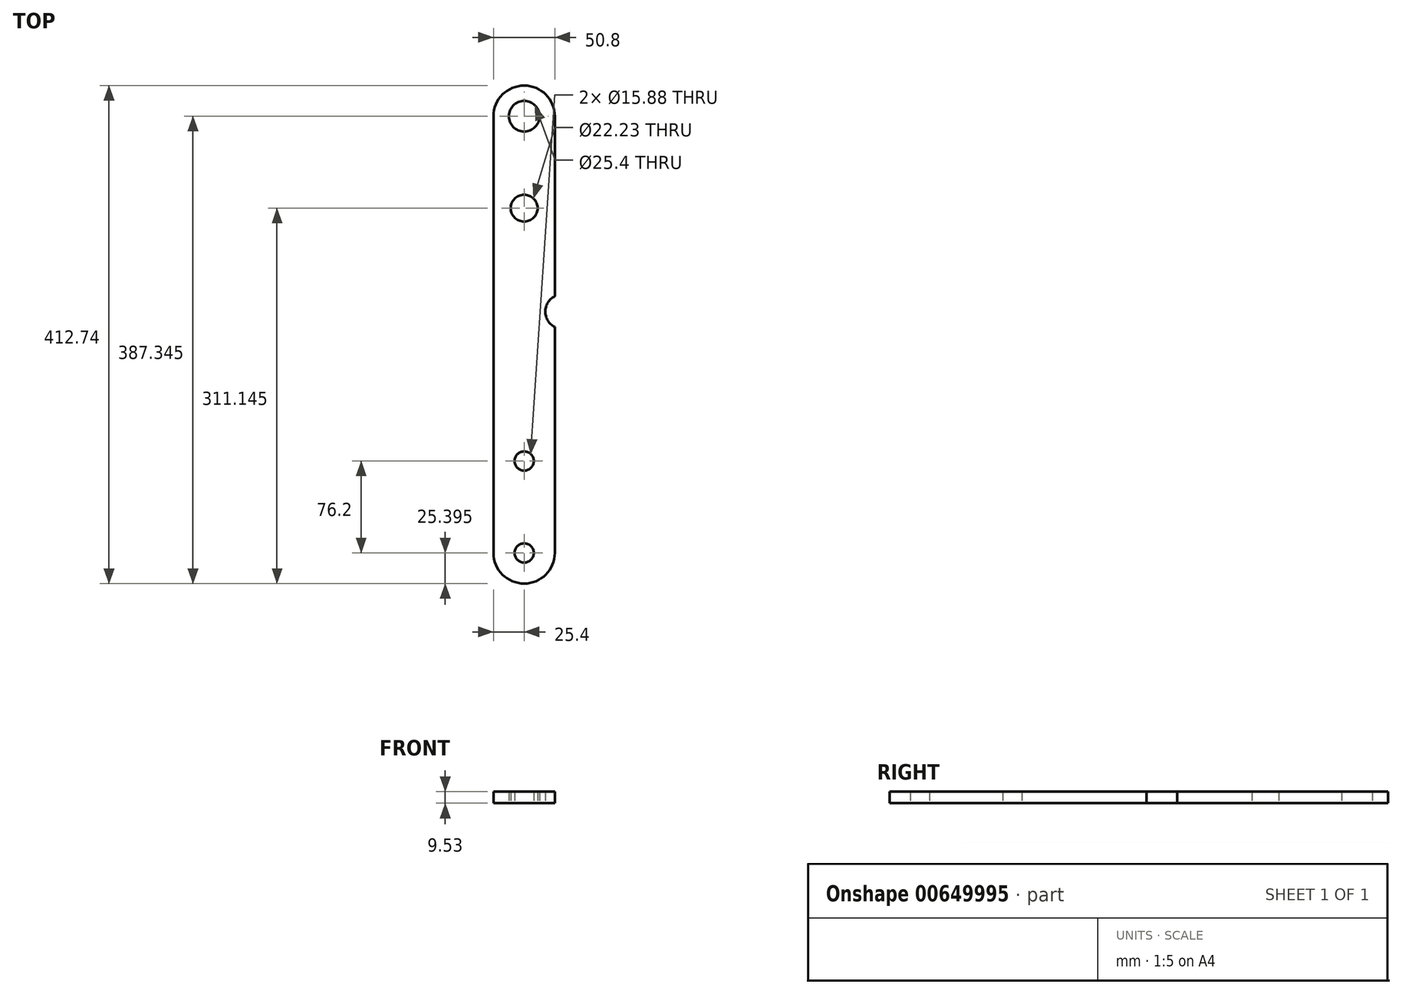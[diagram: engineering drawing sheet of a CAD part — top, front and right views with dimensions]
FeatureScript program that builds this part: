
annotation { "Feature Type Name" : "Feature", "Feature Type Description" : "" }
export const myFeature = defineFeature(function(context is Context, id is Id, definition is map)
    precondition{}
    {
        {
            var Q0;
            Q0=qCreatedBy(makeId("Top.planeOp"),FACE);
            var sketch = newSketch(context, id + "F0", { "sketchPlane" : qUnion([Q0])});
            skLineSegment(sketch, "E0", {"start": v(25.4, 180.98) * mm, "end": v(25.36, 182.46) * mm});
            skLineSegment(sketch, "E1", {"start": v(25.36, 182.46) * mm, "end": v(25.23, 183.94) * mm});
            skLineSegment(sketch, "E2", {"start": v(25.23, 183.94) * mm, "end": v(25.02, 185.4) * mm});
            skLineSegment(sketch, "E3", {"start": v(25.02, 185.4) * mm, "end": v(24.72, 186.84) * mm});
            skLineSegment(sketch, "E4", {"start": v(24.72, 186.84) * mm, "end": v(24.34, 188.26) * mm});
            skLineSegment(sketch, "E5", {"start": v(24.34, 188.26) * mm, "end": v(23.88, 189.67) * mm});
            skLineSegment(sketch, "E6", {"start": v(23.88, 189.67) * mm, "end": v(23.33, 191.05) * mm});
            skLineSegment(sketch, "E7", {"start": v(23.33, 191.05) * mm, "end": v(22.71, 192.38) * mm});
            skLineSegment(sketch, "E8", {"start": v(22.71, 192.38) * mm, "end": v(22, 193.68) * mm});
            skLineSegment(sketch, "E9", {"start": v(22, 193.68) * mm, "end": v(21.23, 194.94) * mm});
            skLineSegment(sketch, "E10", {"start": v(21.23, 194.94) * mm, "end": v(20.38, 196.15) * mm});
            skLineSegment(sketch, "E11", {"start": v(20.38, 196.15) * mm, "end": v(19.45, 197.32) * mm});
            skLineSegment(sketch, "E12", {"start": v(19.45, 197.32) * mm, "end": v(18.48, 198.42) * mm});
            skLineSegment(sketch, "E13", {"start": v(18.48, 198.42) * mm, "end": v(17.44, 199.45) * mm});
            skLineSegment(sketch, "E14", {"start": v(17.44, 199.45) * mm, "end": v(16.34, 200.45) * mm});
            skLineSegment(sketch, "E15", {"start": v(16.34, 200.45) * mm, "end": v(15.18, 201.36) * mm});
            skLineSegment(sketch, "E16", {"start": v(15.18, 201.36) * mm, "end": v(13.97, 202.2) * mm});
            skLineSegment(sketch, "E17", {"start": v(13.97, 202.2) * mm, "end": v(12.7, 202.97) * mm});
            skLineSegment(sketch, "E18", {"start": v(12.7, 202.97) * mm, "end": v(11.4, 203.69) * mm});
            skLineSegment(sketch, "E19", {"start": v(11.4, 203.69) * mm, "end": v(10.08, 204.3) * mm});
            skLineSegment(sketch, "E20", {"start": v(10.08, 204.3) * mm, "end": v(8.7, 204.85) * mm});
            skLineSegment(sketch, "E21", {"start": v(8.7, 204.85) * mm, "end": v(7.28, 205.32) * mm});
            skLineSegment(sketch, "E22", {"start": v(7.28, 205.32) * mm, "end": v(5.86, 205.7) * mm});
            skLineSegment(sketch, "E23", {"start": v(5.86, 205.7) * mm, "end": v(4.42, 206) * mm});
            skLineSegment(sketch, "E24", {"start": v(4.42, 206) * mm, "end": v(2.96, 206.2) * mm});
            skLineSegment(sketch, "E25", {"start": v(2.96, 206.2) * mm, "end": v(1.48, 206.33) * mm});
            skLineSegment(sketch, "E26", {"start": v(1.48, 206.33) * mm, "end": v(0, 206.38) * mm});
            skLineSegment(sketch, "E27", {"start": v(0, 206.38) * mm, "end": v(-1.48, 206.33) * mm});
            skLineSegment(sketch, "E28", {"start": v(-1.48, 206.33) * mm, "end": v(-2.94, 206.2) * mm});
            skLineSegment(sketch, "E29", {"start": v(-2.94, 206.2) * mm, "end": v(-4.4, 206) * mm});
            skLineSegment(sketch, "E30", {"start": v(-4.4, 206) * mm, "end": v(-5.86, 205.7) * mm});
            skLineSegment(sketch, "E31", {"start": v(-5.86, 205.7) * mm, "end": v(-7.28, 205.32) * mm});
            skLineSegment(sketch, "E32", {"start": v(-7.28, 205.32) * mm, "end": v(-8.68, 204.85) * mm});
            skLineSegment(sketch, "E33", {"start": v(-8.68, 204.85) * mm, "end": v(-10.05, 204.3) * mm});
            skLineSegment(sketch, "E34", {"start": v(-10.05, 204.3) * mm, "end": v(-11.39, 203.69) * mm});
            skLineSegment(sketch, "E35", {"start": v(-11.39, 203.69) * mm, "end": v(-12.7, 202.97) * mm});
            skLineSegment(sketch, "E36", {"start": v(-12.7, 202.97) * mm, "end": v(-13.95, 202.2) * mm});
            skLineSegment(sketch, "E37", {"start": v(-13.95, 202.2) * mm, "end": v(-15.16, 201.36) * mm});
            skLineSegment(sketch, "E38", {"start": v(-15.16, 201.36) * mm, "end": v(-16.32, 200.45) * mm});
            skLineSegment(sketch, "E39", {"start": v(-16.32, 200.45) * mm, "end": v(-17.42, 199.45) * mm});
            skLineSegment(sketch, "E40", {"start": v(-17.42, 199.45) * mm, "end": v(-18.48, 198.42) * mm});
            skLineSegment(sketch, "E41", {"start": v(-18.48, 198.42) * mm, "end": v(-19.45, 197.32) * mm});
            skLineSegment(sketch, "E42", {"start": v(-19.45, 197.32) * mm, "end": v(-20.36, 196.15) * mm});
            skLineSegment(sketch, "E43", {"start": v(-20.36, 196.15) * mm, "end": v(-21.2, 194.94) * mm});
            skLineSegment(sketch, "E44", {"start": v(-21.2, 194.94) * mm, "end": v(-22, 193.68) * mm});
            skLineSegment(sketch, "E45", {"start": v(-22, 193.68) * mm, "end": v(-22.7, 192.38) * mm});
            skLineSegment(sketch, "E46", {"start": v(-22.7, 192.38) * mm, "end": v(-23.33, 191.05) * mm});
            skLineSegment(sketch, "E47", {"start": v(-23.33, 191.05) * mm, "end": v(-23.85, 189.67) * mm});
            skLineSegment(sketch, "E48", {"start": v(-23.85, 189.67) * mm, "end": v(-24.32, 188.26) * mm});
            skLineSegment(sketch, "E49", {"start": v(-24.32, 188.26) * mm, "end": v(-24.7, 186.84) * mm});
            skLineSegment(sketch, "E50", {"start": v(-24.7, 186.84) * mm, "end": v(-25.02, 185.4) * mm});
            skLineSegment(sketch, "E51", {"start": v(-25.02, 185.4) * mm, "end": v(-25.23, 183.94) * mm});
            skLineSegment(sketch, "E52", {"start": v(-25.23, 183.94) * mm, "end": v(-25.36, 182.46) * mm});
            skLineSegment(sketch, "E53", {"start": v(-25.36, 182.46) * mm, "end": v(-25.4, 180.98) * mm});
            skLineSegment(sketch, "E54", {"start": v(0, 168.28) * mm, "end": v(1.06, 168.32) * mm});
            skLineSegment(sketch, "E55", {"start": v(1.06, 168.32) * mm, "end": v(2.1, 168.44) * mm});
            skLineSegment(sketch, "E56", {"start": v(2.1, 168.44) * mm, "end": v(3.11, 168.68) * mm});
            skLineSegment(sketch, "E57", {"start": v(3.11, 168.68) * mm, "end": v(4.13, 168.97) * mm});
            skLineSegment(sketch, "E58", {"start": v(4.13, 168.97) * mm, "end": v(5.1, 169.35) * mm});
            skLineSegment(sketch, "E59", {"start": v(5.1, 169.35) * mm, "end": v(6.05, 169.82) * mm});
            skLineSegment(sketch, "E60", {"start": v(6.05, 169.82) * mm, "end": v(6.94, 170.35) * mm});
            skLineSegment(sketch, "E61", {"start": v(6.94, 170.35) * mm, "end": v(7.81, 170.96) * mm});
            skLineSegment(sketch, "E62", {"start": v(7.81, 170.96) * mm, "end": v(8.61, 171.64) * mm});
            skLineSegment(sketch, "E63", {"start": v(8.61, 171.64) * mm, "end": v(9.36, 172.38) * mm});
            skLineSegment(sketch, "E64", {"start": v(9.36, 172.38) * mm, "end": v(10.03, 173.19) * mm});
            skLineSegment(sketch, "E65", {"start": v(10.03, 173.19) * mm, "end": v(10.65, 174.03) * mm});
            skLineSegment(sketch, "E66", {"start": v(10.65, 174.03) * mm, "end": v(11.18, 174.94) * mm});
            skLineSegment(sketch, "E67", {"start": v(11.18, 174.94) * mm, "end": v(11.64, 175.87) * mm});
            skLineSegment(sketch, "E68", {"start": v(11.64, 175.87) * mm, "end": v(12.02, 176.85) * mm});
            skLineSegment(sketch, "E69", {"start": v(12.02, 176.85) * mm, "end": v(12.32, 177.86) * mm});
            skLineSegment(sketch, "E70", {"start": v(12.32, 177.86) * mm, "end": v(12.53, 178.88) * mm});
            skLineSegment(sketch, "E71", {"start": v(12.53, 178.88) * mm, "end": v(12.66, 179.94) * mm});
            skLineSegment(sketch, "E72", {"start": v(12.66, 179.94) * mm, "end": v(12.7, 180.98) * mm});
            skLineSegment(sketch, "E73", {"start": v(12.7, 180.98) * mm, "end": v(12.66, 182.03) * mm});
            skLineSegment(sketch, "E74", {"start": v(12.66, 182.03) * mm, "end": v(12.53, 183.07) * mm});
            skLineSegment(sketch, "E75", {"start": v(12.53, 183.07) * mm, "end": v(12.32, 184.1) * mm});
            skLineSegment(sketch, "E76", {"start": v(12.32, 184.1) * mm, "end": v(12.02, 185.1) * mm});
            skLineSegment(sketch, "E77", {"start": v(12.02, 185.1) * mm, "end": v(11.64, 186.08) * mm});
            skLineSegment(sketch, "E78", {"start": v(11.64, 186.08) * mm, "end": v(11.18, 187.03) * mm});
            skLineSegment(sketch, "E79", {"start": v(11.18, 187.03) * mm, "end": v(10.65, 187.92) * mm});
            skLineSegment(sketch, "E80", {"start": v(10.65, 187.92) * mm, "end": v(10.03, 188.79) * mm});
            skLineSegment(sketch, "E81", {"start": v(10.03, 188.79) * mm, "end": v(9.36, 189.59) * mm});
            skLineSegment(sketch, "E82", {"start": v(9.36, 189.59) * mm, "end": v(8.61, 190.33) * mm});
            skLineSegment(sketch, "E83", {"start": v(8.61, 190.33) * mm, "end": v(7.81, 191) * mm});
            skLineSegment(sketch, "E84", {"start": v(7.81, 191) * mm, "end": v(6.94, 191.62) * mm});
            skLineSegment(sketch, "E85", {"start": v(6.94, 191.62) * mm, "end": v(6.05, 192.15) * mm});
            skLineSegment(sketch, "E86", {"start": v(6.05, 192.15) * mm, "end": v(5.1, 192.62) * mm});
            skLineSegment(sketch, "E87", {"start": v(5.1, 192.62) * mm, "end": v(4.13, 193) * mm});
            skLineSegment(sketch, "E88", {"start": v(4.13, 193) * mm, "end": v(3.11, 193.3) * mm});
            skLineSegment(sketch, "E89", {"start": v(3.11, 193.3) * mm, "end": v(2.1, 193.5) * mm});
            skLineSegment(sketch, "E90", {"start": v(2.1, 193.5) * mm, "end": v(1.06, 193.63) * mm});
            skLineSegment(sketch, "E91", {"start": v(1.06, 193.63) * mm, "end": v(0, 193.68) * mm});
            skLineSegment(sketch, "E92", {"start": v(0, 193.68) * mm, "end": v(-1.04, 193.63) * mm});
            skLineSegment(sketch, "E93", {"start": v(-1.04, 193.63) * mm, "end": v(-2.1, 193.5) * mm});
            skLineSegment(sketch, "E94", {"start": v(-2.1, 193.5) * mm, "end": v(-3.11, 193.3) * mm});
            skLineSegment(sketch, "E95", {"start": v(-3.11, 193.3) * mm, "end": v(-4.13, 193) * mm});
            skLineSegment(sketch, "E96", {"start": v(-4.13, 193) * mm, "end": v(-5.1, 192.62) * mm});
            skLineSegment(sketch, "E97", {"start": v(-5.1, 192.62) * mm, "end": v(-6.03, 192.15) * mm});
            skLineSegment(sketch, "E98", {"start": v(-6.03, 192.15) * mm, "end": v(-6.94, 191.62) * mm});
            skLineSegment(sketch, "E99", {"start": v(-6.94, 191.62) * mm, "end": v(-7.79, 191) * mm});
            skLineSegment(sketch, "E100", {"start": v(-7.79, 191) * mm, "end": v(-8.6, 190.33) * mm});
            skLineSegment(sketch, "E101", {"start": v(-8.6, 190.33) * mm, "end": v(-9.33, 189.59) * mm});
            skLineSegment(sketch, "E102", {"start": v(-9.33, 189.59) * mm, "end": v(-10.01, 188.79) * mm});
            skLineSegment(sketch, "E103", {"start": v(-10.01, 188.79) * mm, "end": v(-10.63, 187.92) * mm});
            skLineSegment(sketch, "E104", {"start": v(-10.63, 187.92) * mm, "end": v(-11.15, 187.03) * mm});
            skLineSegment(sketch, "E105", {"start": v(-11.15, 187.03) * mm, "end": v(-11.62, 186.08) * mm});
            skLineSegment(sketch, "E106", {"start": v(-11.62, 186.08) * mm, "end": v(-12, 185.1) * mm});
            skLineSegment(sketch, "E107", {"start": v(-12, 185.1) * mm, "end": v(-12.3, 184.1) * mm});
            skLineSegment(sketch, "E108", {"start": v(-12.3, 184.1) * mm, "end": v(-12.53, 183.07) * mm});
            skLineSegment(sketch, "E109", {"start": v(-12.53, 183.07) * mm, "end": v(-12.66, 182.03) * mm});
            skLineSegment(sketch, "E110", {"start": v(-12.66, 182.03) * mm, "end": v(-12.7, 180.98) * mm});
            skLineSegment(sketch, "E111", {"start": v(-12.7, 180.98) * mm, "end": v(-12.66, 179.94) * mm});
            skLineSegment(sketch, "E112", {"start": v(-12.66, 179.94) * mm, "end": v(-12.53, 178.88) * mm});
            skLineSegment(sketch, "E113", {"start": v(-12.53, 178.88) * mm, "end": v(-12.3, 177.86) * mm});
            skLineSegment(sketch, "E114", {"start": v(-12.3, 177.86) * mm, "end": v(-12, 176.85) * mm});
            skLineSegment(sketch, "E115", {"start": v(-12, 176.85) * mm, "end": v(-11.62, 175.87) * mm});
            skLineSegment(sketch, "E116", {"start": v(-11.62, 175.87) * mm, "end": v(-11.15, 174.94) * mm});
            skLineSegment(sketch, "E117", {"start": v(-11.15, 174.94) * mm, "end": v(-10.63, 174.03) * mm});
            skLineSegment(sketch, "E118", {"start": v(-10.63, 174.03) * mm, "end": v(-10.01, 173.19) * mm});
            skLineSegment(sketch, "E119", {"start": v(-10.01, 173.19) * mm, "end": v(-9.33, 172.38) * mm});
            skLineSegment(sketch, "E120", {"start": v(-9.33, 172.38) * mm, "end": v(-8.6, 171.64) * mm});
            skLineSegment(sketch, "E121", {"start": v(-8.6, 171.64) * mm, "end": v(-7.79, 170.96) * mm});
            skLineSegment(sketch, "E122", {"start": v(-7.79, 170.96) * mm, "end": v(-6.94, 170.35) * mm});
            skLineSegment(sketch, "E123", {"start": v(-6.94, 170.35) * mm, "end": v(-6.03, 169.82) * mm});
            skLineSegment(sketch, "E124", {"start": v(-6.03, 169.82) * mm, "end": v(-5.1, 169.35) * mm});
            skLineSegment(sketch, "E125", {"start": v(-5.1, 169.35) * mm, "end": v(-4.13, 168.97) * mm});
            skLineSegment(sketch, "E126", {"start": v(-4.13, 168.97) * mm, "end": v(-3.11, 168.68) * mm});
            skLineSegment(sketch, "E127", {"start": v(-3.11, 168.68) * mm, "end": v(-2.1, 168.44) * mm});
            skLineSegment(sketch, "E128", {"start": v(-2.1, 168.44) * mm, "end": v(-1.04, 168.32) * mm});
            skLineSegment(sketch, "E129", {"start": v(-1.04, 168.32) * mm, "end": v(0, 168.28) * mm});
            skLineSegment(sketch, "E130", {"start": v(25.4, 6.35) * mm, "end": v(25.4, -180.98) * mm});
            skLineSegment(sketch, "E131", {"start": v(25.4, 180.98) * mm, "end": v(25.4, 31.75) * mm});
            skLineSegment(sketch, "E132", {"start": v(-25.4, 180.98) * mm, "end": v(-25.4, -180.98) * mm});
            skLineSegment(sketch, "E133", {"start": v(0, -188.91) * mm, "end": v(0.83, -188.87) * mm});
            skLineSegment(sketch, "E134", {"start": v(0.83, -188.87) * mm, "end": v(1.65, -188.74) * mm});
            skLineSegment(sketch, "E135", {"start": v(1.65, -188.74) * mm, "end": v(2.46, -188.51) * mm});
            skLineSegment(sketch, "E136", {"start": v(2.46, -188.51) * mm, "end": v(3.24, -188.21) * mm});
            skLineSegment(sketch, "E137", {"start": v(3.24, -188.21) * mm, "end": v(3.98, -187.85) * mm});
            skLineSegment(sketch, "E138", {"start": v(3.98, -187.85) * mm, "end": v(4.68, -187.39) * mm});
            skLineSegment(sketch, "E139", {"start": v(4.68, -187.39) * mm, "end": v(5.31, -186.86) * mm});
            skLineSegment(sketch, "E140", {"start": v(5.31, -186.86) * mm, "end": v(5.9, -186.29) * mm});
            skLineSegment(sketch, "E141", {"start": v(5.9, -186.29) * mm, "end": v(6.43, -185.63) * mm});
            skLineSegment(sketch, "E142", {"start": v(6.43, -185.63) * mm, "end": v(6.88, -184.93) * mm});
            skLineSegment(sketch, "E143", {"start": v(6.88, -184.93) * mm, "end": v(7.26, -184.2) * mm});
            skLineSegment(sketch, "E144", {"start": v(7.26, -184.2) * mm, "end": v(7.56, -183.43) * mm});
            skLineSegment(sketch, "E145", {"start": v(7.56, -183.43) * mm, "end": v(7.77, -182.63) * mm});
            skLineSegment(sketch, "E146", {"start": v(7.77, -182.63) * mm, "end": v(7.9, -181.8) * mm});
            skLineSegment(sketch, "E147", {"start": v(7.9, -181.8) * mm, "end": v(7.94, -180.98) * mm});
            skLineSegment(sketch, "E148", {"start": v(7.94, -180.98) * mm, "end": v(7.9, -180.15) * mm});
            skLineSegment(sketch, "E149", {"start": v(7.9, -180.15) * mm, "end": v(7.77, -179.32) * mm});
            skLineSegment(sketch, "E150", {"start": v(7.77, -179.32) * mm, "end": v(7.56, -178.52) * mm});
            skLineSegment(sketch, "E151", {"start": v(7.56, -178.52) * mm, "end": v(7.26, -177.74) * mm});
            skLineSegment(sketch, "E152", {"start": v(7.26, -177.74) * mm, "end": v(6.88, -177) * mm});
            skLineSegment(sketch, "E153", {"start": v(6.88, -177) * mm, "end": v(6.43, -176.3) * mm});
            skLineSegment(sketch, "E154", {"start": v(6.43, -176.3) * mm, "end": v(5.9, -175.66) * mm});
            skLineSegment(sketch, "E155", {"start": v(5.9, -175.66) * mm, "end": v(5.31, -175.07) * mm});
            skLineSegment(sketch, "E156", {"start": v(5.31, -175.07) * mm, "end": v(4.68, -174.54) * mm});
            skLineSegment(sketch, "E157", {"start": v(4.68, -174.54) * mm, "end": v(3.98, -174.1) * mm});
            skLineSegment(sketch, "E158", {"start": v(3.98, -174.1) * mm, "end": v(3.24, -173.71) * mm});
            skLineSegment(sketch, "E159", {"start": v(3.24, -173.71) * mm, "end": v(2.46, -173.42) * mm});
            skLineSegment(sketch, "E160", {"start": v(2.46, -173.42) * mm, "end": v(1.65, -173.2) * mm});
            skLineSegment(sketch, "E161", {"start": v(1.65, -173.2) * mm, "end": v(0.83, -173.08) * mm});
            skLineSegment(sketch, "E162", {"start": v(0.83, -173.08) * mm, "end": v(0, -173.04) * mm});
            skLineSegment(sketch, "E163", {"start": v(0, -173.04) * mm, "end": v(-0.83, -173.08) * mm});
            skLineSegment(sketch, "E164", {"start": v(-0.83, -173.08) * mm, "end": v(-1.65, -173.2) * mm});
            skLineSegment(sketch, "E165", {"start": v(-1.65, -173.2) * mm, "end": v(-2.46, -173.42) * mm});
            skLineSegment(sketch, "E166", {"start": v(-2.46, -173.42) * mm, "end": v(-3.22, -173.71) * mm});
            skLineSegment(sketch, "E167", {"start": v(-3.22, -173.71) * mm, "end": v(-3.96, -174.1) * mm});
            skLineSegment(sketch, "E168", {"start": v(-3.96, -174.1) * mm, "end": v(-4.66, -174.54) * mm});
            skLineSegment(sketch, "E169", {"start": v(-4.66, -174.54) * mm, "end": v(-5.31, -175.07) * mm});
            skLineSegment(sketch, "E170", {"start": v(-5.31, -175.07) * mm, "end": v(-5.88, -175.66) * mm});
            skLineSegment(sketch, "E171", {"start": v(-5.88, -175.66) * mm, "end": v(-6.41, -176.3) * mm});
            skLineSegment(sketch, "E172", {"start": v(-6.41, -176.3) * mm, "end": v(-6.88, -177) * mm});
            skLineSegment(sketch, "E173", {"start": v(-6.88, -177) * mm, "end": v(-7.24, -177.74) * mm});
            skLineSegment(sketch, "E174", {"start": v(-7.24, -177.74) * mm, "end": v(-7.54, -178.52) * mm});
            skLineSegment(sketch, "E175", {"start": v(-7.54, -178.52) * mm, "end": v(-7.77, -179.32) * mm});
            skLineSegment(sketch, "E176", {"start": v(-7.77, -179.32) * mm, "end": v(-7.9, -180.15) * mm});
            skLineSegment(sketch, "E177", {"start": v(-7.9, -180.15) * mm, "end": v(-7.94, -180.98) * mm});
            skLineSegment(sketch, "E178", {"start": v(-7.94, -180.98) * mm, "end": v(-7.9, -181.8) * mm});
            skLineSegment(sketch, "E179", {"start": v(-7.9, -181.8) * mm, "end": v(-7.77, -182.63) * mm});
            skLineSegment(sketch, "E180", {"start": v(-7.77, -182.63) * mm, "end": v(-7.54, -183.43) * mm});
            skLineSegment(sketch, "E181", {"start": v(-7.54, -183.43) * mm, "end": v(-7.24, -184.2) * mm});
            skLineSegment(sketch, "E182", {"start": v(-7.24, -184.2) * mm, "end": v(-6.88, -184.93) * mm});
            skLineSegment(sketch, "E183", {"start": v(-6.88, -184.93) * mm, "end": v(-6.41, -185.63) * mm});
            skLineSegment(sketch, "E184", {"start": v(-6.41, -185.63) * mm, "end": v(-5.88, -186.29) * mm});
            skLineSegment(sketch, "E185", {"start": v(-5.88, -186.29) * mm, "end": v(-5.31, -186.86) * mm});
            skLineSegment(sketch, "E186", {"start": v(-5.31, -186.86) * mm, "end": v(-4.66, -187.39) * mm});
            skLineSegment(sketch, "E187", {"start": v(-4.66, -187.39) * mm, "end": v(-3.96, -187.85) * mm});
            skLineSegment(sketch, "E188", {"start": v(-3.96, -187.85) * mm, "end": v(-3.22, -188.21) * mm});
            skLineSegment(sketch, "E189", {"start": v(-3.22, -188.21) * mm, "end": v(-2.46, -188.51) * mm});
            skLineSegment(sketch, "E190", {"start": v(-2.46, -188.51) * mm, "end": v(-1.65, -188.74) * mm});
            skLineSegment(sketch, "E191", {"start": v(-1.65, -188.74) * mm, "end": v(-0.83, -188.87) * mm});
            skLineSegment(sketch, "E192", {"start": v(-0.83, -188.87) * mm, "end": v(0, -188.91) * mm});
            skLineSegment(sketch, "E193", {"start": v(-25.4, -180.98) * mm, "end": v(-25.36, -182.46) * mm});
            skLineSegment(sketch, "E194", {"start": v(-25.36, -182.46) * mm, "end": v(-25.23, -183.92) * mm});
            skLineSegment(sketch, "E195", {"start": v(-25.23, -183.92) * mm, "end": v(-25.02, -185.38) * mm});
            skLineSegment(sketch, "E196", {"start": v(-25.02, -185.38) * mm, "end": v(-24.7, -186.82) * mm});
            skLineSegment(sketch, "E197", {"start": v(-24.7, -186.82) * mm, "end": v(-24.32, -188.26) * mm});
            skLineSegment(sketch, "E198", {"start": v(-24.32, -188.26) * mm, "end": v(-23.85, -189.65) * mm});
            skLineSegment(sketch, "E199", {"start": v(-23.85, -189.65) * mm, "end": v(-23.33, -191.03) * mm});
            skLineSegment(sketch, "E200", {"start": v(-23.33, -191.03) * mm, "end": v(-22.7, -192.36) * mm});
            skLineSegment(sketch, "E201", {"start": v(-22.7, -192.36) * mm, "end": v(-22, -193.68) * mm});
            skLineSegment(sketch, "E202", {"start": v(-22, -193.68) * mm, "end": v(-21.2, -194.92) * mm});
            skLineSegment(sketch, "E203", {"start": v(-21.2, -194.92) * mm, "end": v(-20.36, -196.13) * mm});
            skLineSegment(sketch, "E204", {"start": v(-20.36, -196.13) * mm, "end": v(-19.45, -197.3) * mm});
            skLineSegment(sketch, "E205", {"start": v(-19.45, -197.3) * mm, "end": v(-18.48, -198.4) * mm});
            skLineSegment(sketch, "E206", {"start": v(-18.48, -198.4) * mm, "end": v(-17.42, -199.45) * mm});
            skLineSegment(sketch, "E207", {"start": v(-17.42, -199.45) * mm, "end": v(-16.32, -200.43) * mm});
            skLineSegment(sketch, "E208", {"start": v(-16.32, -200.43) * mm, "end": v(-15.16, -201.34) * mm});
            skLineSegment(sketch, "E209", {"start": v(-15.16, -201.34) * mm, "end": v(-13.95, -202.18) * mm});
            skLineSegment(sketch, "E210", {"start": v(-13.95, -202.18) * mm, "end": v(-12.7, -202.97) * mm});
            skLineSegment(sketch, "E211", {"start": v(-12.7, -202.97) * mm, "end": v(-11.39, -203.67) * mm});
            skLineSegment(sketch, "E212", {"start": v(-11.39, -203.67) * mm, "end": v(-10.05, -204.3) * mm});
            skLineSegment(sketch, "E213", {"start": v(-10.05, -204.3) * mm, "end": v(-8.68, -204.83) * mm});
            skLineSegment(sketch, "E214", {"start": v(-8.68, -204.83) * mm, "end": v(-7.28, -205.3) * mm});
            skLineSegment(sketch, "E215", {"start": v(-7.28, -205.3) * mm, "end": v(-5.86, -205.68) * mm});
            skLineSegment(sketch, "E216", {"start": v(-5.86, -205.68) * mm, "end": v(-4.4, -206) * mm});
            skLineSegment(sketch, "E217", {"start": v(-4.4, -206) * mm, "end": v(-2.94, -206.2) * mm});
            skLineSegment(sketch, "E218", {"start": v(-2.94, -206.2) * mm, "end": v(-1.48, -206.33) * mm});
            skLineSegment(sketch, "E219", {"start": v(-1.48, -206.33) * mm, "end": v(0, -206.38) * mm});
            skLineSegment(sketch, "E220", {"start": v(0, -206.38) * mm, "end": v(1.48, -206.33) * mm});
            skLineSegment(sketch, "E221", {"start": v(1.48, -206.33) * mm, "end": v(2.96, -206.2) * mm});
            skLineSegment(sketch, "E222", {"start": v(2.96, -206.2) * mm, "end": v(4.42, -206) * mm});
            skLineSegment(sketch, "E223", {"start": v(4.42, -206) * mm, "end": v(5.86, -205.68) * mm});
            skLineSegment(sketch, "E224", {"start": v(5.86, -205.68) * mm, "end": v(7.28, -205.3) * mm});
            skLineSegment(sketch, "E225", {"start": v(7.28, -205.3) * mm, "end": v(8.7, -204.83) * mm});
            skLineSegment(sketch, "E226", {"start": v(8.7, -204.83) * mm, "end": v(10.08, -204.3) * mm});
            skLineSegment(sketch, "E227", {"start": v(10.08, -204.3) * mm, "end": v(11.4, -203.67) * mm});
            skLineSegment(sketch, "E228", {"start": v(11.4, -203.67) * mm, "end": v(12.7, -202.97) * mm});
            skLineSegment(sketch, "E229", {"start": v(12.7, -202.97) * mm, "end": v(13.97, -202.18) * mm});
            skLineSegment(sketch, "E230", {"start": v(13.97, -202.18) * mm, "end": v(15.18, -201.34) * mm});
            skLineSegment(sketch, "E231", {"start": v(15.18, -201.34) * mm, "end": v(16.34, -200.43) * mm});
            skLineSegment(sketch, "E232", {"start": v(16.34, -200.43) * mm, "end": v(17.44, -199.45) * mm});
            skLineSegment(sketch, "E233", {"start": v(17.44, -199.45) * mm, "end": v(18.48, -198.4) * mm});
            skLineSegment(sketch, "E234", {"start": v(18.48, -198.4) * mm, "end": v(19.45, -197.3) * mm});
            skLineSegment(sketch, "E235", {"start": v(19.45, -197.3) * mm, "end": v(20.38, -196.13) * mm});
            skLineSegment(sketch, "E236", {"start": v(20.38, -196.13) * mm, "end": v(21.23, -194.92) * mm});
            skLineSegment(sketch, "E237", {"start": v(21.23, -194.92) * mm, "end": v(22, -193.68) * mm});
            skLineSegment(sketch, "E238", {"start": v(22, -193.68) * mm, "end": v(22.71, -192.36) * mm});
            skLineSegment(sketch, "E239", {"start": v(22.71, -192.36) * mm, "end": v(23.33, -191.03) * mm});
            skLineSegment(sketch, "E240", {"start": v(23.33, -191.03) * mm, "end": v(23.88, -189.65) * mm});
            skLineSegment(sketch, "E241", {"start": v(23.88, -189.65) * mm, "end": v(24.34, -188.26) * mm});
            skLineSegment(sketch, "E242", {"start": v(24.34, -188.26) * mm, "end": v(24.72, -186.82) * mm});
            skLineSegment(sketch, "E243", {"start": v(24.72, -186.82) * mm, "end": v(25.02, -185.38) * mm});
            skLineSegment(sketch, "E244", {"start": v(25.02, -185.38) * mm, "end": v(25.23, -183.92) * mm});
            skLineSegment(sketch, "E245", {"start": v(25.23, -183.92) * mm, "end": v(25.36, -182.46) * mm});
            skLineSegment(sketch, "E246", {"start": v(25.36, -182.46) * mm, "end": v(25.4, -180.98) * mm});
            skLineSegment(sketch, "E247", {"start": v(0, 93.66) * mm, "end": v(0.97, 93.7) * mm});
            skLineSegment(sketch, "E248", {"start": v(0.97, 93.7) * mm, "end": v(1.93, 93.83) * mm});
            skLineSegment(sketch, "E249", {"start": v(1.93, 93.83) * mm, "end": v(2.88, 94.04) * mm});
            skLineSegment(sketch, "E250", {"start": v(2.88, 94.04) * mm, "end": v(3.8, 94.34) * mm});
            skLineSegment(sketch, "E251", {"start": v(3.8, 94.34) * mm, "end": v(4.7, 94.7) * mm});
            skLineSegment(sketch, "E252", {"start": v(4.7, 94.7) * mm, "end": v(5.57, 95.17) * mm});
            skLineSegment(sketch, "E253", {"start": v(5.57, 95.17) * mm, "end": v(6.37, 95.67) * mm});
            skLineSegment(sketch, "E254", {"start": v(6.37, 95.67) * mm, "end": v(7.15, 96.27) * mm});
            skLineSegment(sketch, "E255", {"start": v(7.15, 96.27) * mm, "end": v(7.85, 96.92) * mm});
            skLineSegment(sketch, "E256", {"start": v(7.85, 96.92) * mm, "end": v(8.5, 97.64) * mm});
            skLineSegment(sketch, "E257", {"start": v(8.5, 97.64) * mm, "end": v(9.1, 98.4) * mm});
            skLineSegment(sketch, "E258", {"start": v(9.1, 98.4) * mm, "end": v(9.63, 99.23) * mm});
            skLineSegment(sketch, "E259", {"start": v(9.63, 99.23) * mm, "end": v(10.08, 100.08) * mm});
            skLineSegment(sketch, "E260", {"start": v(10.08, 100.08) * mm, "end": v(10.46, 100.99) * mm});
            skLineSegment(sketch, "E261", {"start": v(10.46, 100.99) * mm, "end": v(10.73, 101.9) * mm});
            skLineSegment(sketch, "E262", {"start": v(10.73, 101.9) * mm, "end": v(10.94, 102.85) * mm});
            skLineSegment(sketch, "E263", {"start": v(10.94, 102.85) * mm, "end": v(11.07, 103.8) * mm});
            skLineSegment(sketch, "E264", {"start": v(11.07, 103.8) * mm, "end": v(11.11, 104.78) * mm});
            skLineSegment(sketch, "E265", {"start": v(11.11, 104.78) * mm, "end": v(11.07, 105.75) * mm});
            skLineSegment(sketch, "E266", {"start": v(11.07, 105.75) * mm, "end": v(10.94, 106.7) * mm});
            skLineSegment(sketch, "E267", {"start": v(10.94, 106.7) * mm, "end": v(10.73, 107.65) * mm});
            skLineSegment(sketch, "E268", {"start": v(10.73, 107.65) * mm, "end": v(10.46, 108.59) * mm});
            skLineSegment(sketch, "E269", {"start": v(10.46, 108.59) * mm, "end": v(10.08, 109.47) * mm});
            skLineSegment(sketch, "E270", {"start": v(10.08, 109.47) * mm, "end": v(9.63, 110.34) * mm});
            skLineSegment(sketch, "E271", {"start": v(9.63, 110.34) * mm, "end": v(9.1, 111.15) * mm});
            skLineSegment(sketch, "E272", {"start": v(9.1, 111.15) * mm, "end": v(8.5, 111.93) * mm});
            skLineSegment(sketch, "E273", {"start": v(8.5, 111.93) * mm, "end": v(7.85, 112.63) * mm});
            skLineSegment(sketch, "E274", {"start": v(7.85, 112.63) * mm, "end": v(7.15, 113.28) * mm});
            skLineSegment(sketch, "E275", {"start": v(7.15, 113.28) * mm, "end": v(6.37, 113.88) * mm});
            skLineSegment(sketch, "E276", {"start": v(6.37, 113.88) * mm, "end": v(5.57, 114.4) * mm});
            skLineSegment(sketch, "E277", {"start": v(5.57, 114.4) * mm, "end": v(4.7, 114.85) * mm});
            skLineSegment(sketch, "E278", {"start": v(4.7, 114.85) * mm, "end": v(3.8, 115.23) * mm});
            skLineSegment(sketch, "E279", {"start": v(3.8, 115.23) * mm, "end": v(2.88, 115.5) * mm});
            skLineSegment(sketch, "E280", {"start": v(2.88, 115.5) * mm, "end": v(1.93, 115.72) * mm});
            skLineSegment(sketch, "E281", {"start": v(1.93, 115.72) * mm, "end": v(0.97, 115.85) * mm});
            skLineSegment(sketch, "E282", {"start": v(0.97, 115.85) * mm, "end": v(0, 115.89) * mm});
            skLineSegment(sketch, "E283", {"start": v(0, 115.89) * mm, "end": v(-0.97, 115.85) * mm});
            skLineSegment(sketch, "E284", {"start": v(-0.97, 115.85) * mm, "end": v(-1.93, 115.72) * mm});
            skLineSegment(sketch, "E285", {"start": v(-1.93, 115.72) * mm, "end": v(-2.88, 115.5) * mm});
            skLineSegment(sketch, "E286", {"start": v(-2.88, 115.5) * mm, "end": v(-3.79, 115.23) * mm});
            skLineSegment(sketch, "E287", {"start": v(-3.79, 115.23) * mm, "end": v(-4.7, 114.85) * mm});
            skLineSegment(sketch, "E288", {"start": v(-4.7, 114.85) * mm, "end": v(-5.55, 114.4) * mm});
            skLineSegment(sketch, "E289", {"start": v(-5.55, 114.4) * mm, "end": v(-6.37, 113.88) * mm});
            skLineSegment(sketch, "E290", {"start": v(-6.37, 113.88) * mm, "end": v(-7.13, 113.28) * mm});
            skLineSegment(sketch, "E291", {"start": v(-7.13, 113.28) * mm, "end": v(-7.85, 112.63) * mm});
            skLineSegment(sketch, "E292", {"start": v(-7.85, 112.63) * mm, "end": v(-8.5, 111.93) * mm});
            skLineSegment(sketch, "E293", {"start": v(-8.5, 111.93) * mm, "end": v(-9.1, 111.15) * mm});
            skLineSegment(sketch, "E294", {"start": v(-9.1, 111.15) * mm, "end": v(-9.6, 110.34) * mm});
            skLineSegment(sketch, "E295", {"start": v(-9.6, 110.34) * mm, "end": v(-10.08, 109.47) * mm});
            skLineSegment(sketch, "E296", {"start": v(-10.08, 109.47) * mm, "end": v(-10.44, 108.59) * mm});
            skLineSegment(sketch, "E297", {"start": v(-10.44, 108.59) * mm, "end": v(-10.73, 107.65) * mm});
            skLineSegment(sketch, "E298", {"start": v(-10.73, 107.65) * mm, "end": v(-10.94, 106.7) * mm});
            skLineSegment(sketch, "E299", {"start": v(-10.94, 106.7) * mm, "end": v(-11.07, 105.75) * mm});
            skLineSegment(sketch, "E300", {"start": v(-11.07, 105.75) * mm, "end": v(-11.11, 104.78) * mm});
            skLineSegment(sketch, "E301", {"start": v(-11.11, 104.78) * mm, "end": v(-11.07, 103.8) * mm});
            skLineSegment(sketch, "E302", {"start": v(-11.07, 103.8) * mm, "end": v(-10.94, 102.85) * mm});
            skLineSegment(sketch, "E303", {"start": v(-10.94, 102.85) * mm, "end": v(-10.73, 101.9) * mm});
            skLineSegment(sketch, "E304", {"start": v(-10.73, 101.9) * mm, "end": v(-10.44, 100.99) * mm});
            skLineSegment(sketch, "E305", {"start": v(-10.44, 100.99) * mm, "end": v(-10.08, 100.08) * mm});
            skLineSegment(sketch, "E306", {"start": v(-10.08, 100.08) * mm, "end": v(-9.6, 99.23) * mm});
            skLineSegment(sketch, "E307", {"start": v(-9.6, 99.23) * mm, "end": v(-9.1, 98.4) * mm});
            skLineSegment(sketch, "E308", {"start": v(-9.1, 98.4) * mm, "end": v(-8.5, 97.64) * mm});
            skLineSegment(sketch, "E309", {"start": v(-8.5, 97.64) * mm, "end": v(-7.85, 96.92) * mm});
            skLineSegment(sketch, "E310", {"start": v(-7.85, 96.92) * mm, "end": v(-7.13, 96.27) * mm});
            skLineSegment(sketch, "E311", {"start": v(-7.13, 96.27) * mm, "end": v(-6.37, 95.67) * mm});
            skLineSegment(sketch, "E312", {"start": v(-6.37, 95.67) * mm, "end": v(-5.55, 95.17) * mm});
            skLineSegment(sketch, "E313", {"start": v(-5.55, 95.17) * mm, "end": v(-4.7, 94.7) * mm});
            skLineSegment(sketch, "E314", {"start": v(-4.7, 94.7) * mm, "end": v(-3.79, 94.34) * mm});
            skLineSegment(sketch, "E315", {"start": v(-3.79, 94.34) * mm, "end": v(-2.88, 94.04) * mm});
            skLineSegment(sketch, "E316", {"start": v(-2.88, 94.04) * mm, "end": v(-1.93, 93.83) * mm});
            skLineSegment(sketch, "E317", {"start": v(-1.93, 93.83) * mm, "end": v(-0.97, 93.7) * mm});
            skLineSegment(sketch, "E318", {"start": v(-0.97, 93.7) * mm, "end": v(0, 93.66) * mm});
            skLineSegment(sketch, "E319", {"start": v(0, -112.71) * mm, "end": v(0.83, -112.67) * mm});
            skLineSegment(sketch, "E320", {"start": v(0.83, -112.67) * mm, "end": v(1.65, -112.54) * mm});
            skLineSegment(sketch, "E321", {"start": v(1.65, -112.54) * mm, "end": v(2.46, -112.31) * mm});
            skLineSegment(sketch, "E322", {"start": v(2.46, -112.31) * mm, "end": v(3.24, -112.01) * mm});
            skLineSegment(sketch, "E323", {"start": v(3.24, -112.01) * mm, "end": v(3.98, -111.65) * mm});
            skLineSegment(sketch, "E324", {"start": v(3.98, -111.65) * mm, "end": v(4.68, -111.19) * mm});
            skLineSegment(sketch, "E325", {"start": v(4.68, -111.19) * mm, "end": v(5.31, -110.66) * mm});
            skLineSegment(sketch, "E326", {"start": v(5.31, -110.66) * mm, "end": v(5.9, -110.09) * mm});
            skLineSegment(sketch, "E327", {"start": v(5.9, -110.09) * mm, "end": v(6.43, -109.43) * mm});
            skLineSegment(sketch, "E328", {"start": v(6.43, -109.43) * mm, "end": v(6.88, -108.73) * mm});
            skLineSegment(sketch, "E329", {"start": v(6.88, -108.73) * mm, "end": v(7.26, -108) * mm});
            skLineSegment(sketch, "E330", {"start": v(7.26, -108) * mm, "end": v(7.56, -107.23) * mm});
            skLineSegment(sketch, "E331", {"start": v(7.56, -107.23) * mm, "end": v(7.77, -106.43) * mm});
            skLineSegment(sketch, "E332", {"start": v(7.77, -106.43) * mm, "end": v(7.9, -105.6) * mm});
            skLineSegment(sketch, "E333", {"start": v(7.9, -105.6) * mm, "end": v(7.94, -104.78) * mm});
            skLineSegment(sketch, "E334", {"start": v(7.94, -104.78) * mm, "end": v(7.9, -103.95) * mm});
            skLineSegment(sketch, "E335", {"start": v(7.9, -103.95) * mm, "end": v(7.77, -103.12) * mm});
            skLineSegment(sketch, "E336", {"start": v(7.77, -103.12) * mm, "end": v(7.56, -102.32) * mm});
            skLineSegment(sketch, "E337", {"start": v(7.56, -102.32) * mm, "end": v(7.26, -101.54) * mm});
            skLineSegment(sketch, "E338", {"start": v(7.26, -101.54) * mm, "end": v(6.88, -100.8) * mm});
            skLineSegment(sketch, "E339", {"start": v(6.88, -100.8) * mm, "end": v(6.43, -100.1) * mm});
            skLineSegment(sketch, "E340", {"start": v(6.43, -100.1) * mm, "end": v(5.9, -99.46) * mm});
            skLineSegment(sketch, "E341", {"start": v(5.9, -99.46) * mm, "end": v(5.31, -98.87) * mm});
            skLineSegment(sketch, "E342", {"start": v(5.31, -98.87) * mm, "end": v(4.68, -98.34) * mm});
            skLineSegment(sketch, "E343", {"start": v(4.68, -98.34) * mm, "end": v(3.98, -97.9) * mm});
            skLineSegment(sketch, "E344", {"start": v(3.98, -97.9) * mm, "end": v(3.24, -97.51) * mm});
            skLineSegment(sketch, "E345", {"start": v(3.24, -97.51) * mm, "end": v(2.46, -97.22) * mm});
            skLineSegment(sketch, "E346", {"start": v(2.46, -97.22) * mm, "end": v(1.65, -97) * mm});
            skLineSegment(sketch, "E347", {"start": v(1.65, -97) * mm, "end": v(0.83, -96.88) * mm});
            skLineSegment(sketch, "E348", {"start": v(0.83, -96.88) * mm, "end": v(0, -96.84) * mm});
            skLineSegment(sketch, "E349", {"start": v(0, -96.84) * mm, "end": v(-0.83, -96.88) * mm});
            skLineSegment(sketch, "E350", {"start": v(-0.83, -96.88) * mm, "end": v(-1.65, -97) * mm});
            skLineSegment(sketch, "E351", {"start": v(-1.65, -97) * mm, "end": v(-2.46, -97.22) * mm});
            skLineSegment(sketch, "E352", {"start": v(-2.46, -97.22) * mm, "end": v(-3.22, -97.51) * mm});
            skLineSegment(sketch, "E353", {"start": v(-3.22, -97.51) * mm, "end": v(-3.96, -97.9) * mm});
            skLineSegment(sketch, "E354", {"start": v(-3.96, -97.9) * mm, "end": v(-4.66, -98.34) * mm});
            skLineSegment(sketch, "E355", {"start": v(-4.66, -98.34) * mm, "end": v(-5.31, -98.87) * mm});
            skLineSegment(sketch, "E356", {"start": v(-5.31, -98.87) * mm, "end": v(-5.88, -99.46) * mm});
            skLineSegment(sketch, "E357", {"start": v(-5.88, -99.46) * mm, "end": v(-6.41, -100.1) * mm});
            skLineSegment(sketch, "E358", {"start": v(-6.41, -100.1) * mm, "end": v(-6.88, -100.8) * mm});
            skLineSegment(sketch, "E359", {"start": v(-6.88, -100.8) * mm, "end": v(-7.24, -101.54) * mm});
            skLineSegment(sketch, "E360", {"start": v(-7.24, -101.54) * mm, "end": v(-7.54, -102.32) * mm});
            skLineSegment(sketch, "E361", {"start": v(-7.54, -102.32) * mm, "end": v(-7.77, -103.12) * mm});
            skLineSegment(sketch, "E362", {"start": v(-7.77, -103.12) * mm, "end": v(-7.9, -103.95) * mm});
            skLineSegment(sketch, "E363", {"start": v(-7.9, -103.95) * mm, "end": v(-7.94, -104.78) * mm});
            skLineSegment(sketch, "E364", {"start": v(-7.94, -104.78) * mm, "end": v(-7.9, -105.6) * mm});
            skLineSegment(sketch, "E365", {"start": v(-7.9, -105.6) * mm, "end": v(-7.77, -106.43) * mm});
            skLineSegment(sketch, "E366", {"start": v(-7.77, -106.43) * mm, "end": v(-7.54, -107.23) * mm});
            skLineSegment(sketch, "E367", {"start": v(-7.54, -107.23) * mm, "end": v(-7.24, -108) * mm});
            skLineSegment(sketch, "E368", {"start": v(-7.24, -108) * mm, "end": v(-6.88, -108.73) * mm});
            skLineSegment(sketch, "E369", {"start": v(-6.88, -108.73) * mm, "end": v(-6.41, -109.43) * mm});
            skLineSegment(sketch, "E370", {"start": v(-6.41, -109.43) * mm, "end": v(-5.88, -110.09) * mm});
            skLineSegment(sketch, "E371", {"start": v(-5.88, -110.09) * mm, "end": v(-5.31, -110.66) * mm});
            skLineSegment(sketch, "E372", {"start": v(-5.31, -110.66) * mm, "end": v(-4.66, -111.19) * mm});
            skLineSegment(sketch, "E373", {"start": v(-4.66, -111.19) * mm, "end": v(-3.96, -111.65) * mm});
            skLineSegment(sketch, "E374", {"start": v(-3.96, -111.65) * mm, "end": v(-3.22, -112.01) * mm});
            skLineSegment(sketch, "E375", {"start": v(-3.22, -112.01) * mm, "end": v(-2.46, -112.31) * mm});
            skLineSegment(sketch, "E376", {"start": v(-2.46, -112.31) * mm, "end": v(-1.65, -112.54) * mm});
            skLineSegment(sketch, "E377", {"start": v(-1.65, -112.54) * mm, "end": v(-0.83, -112.67) * mm});
            skLineSegment(sketch, "E378", {"start": v(-0.83, -112.67) * mm, "end": v(0, -112.71) * mm});
            skLineSegment(sketch, "E379", {"start": v(25.4, 31.75) * mm, "end": v(24.47, 31.26) * mm});
            skLineSegment(sketch, "E380", {"start": v(24.47, 31.26) * mm, "end": v(23.58, 30.7) * mm});
            skLineSegment(sketch, "E381", {"start": v(23.58, 30.7) * mm, "end": v(22.75, 30.08) * mm});
            skLineSegment(sketch, "E382", {"start": v(22.75, 30.08) * mm, "end": v(21.95, 29.38) * mm});
            skLineSegment(sketch, "E383", {"start": v(21.95, 29.38) * mm, "end": v(21.2, 28.64) * mm});
            skLineSegment(sketch, "E384", {"start": v(21.2, 28.64) * mm, "end": v(20.53, 27.83) * mm});
            skLineSegment(sketch, "E385", {"start": v(20.53, 27.83) * mm, "end": v(19.9, 26.99) * mm});
            skLineSegment(sketch, "E386", {"start": v(19.9, 26.99) * mm, "end": v(19.35, 26.1) * mm});
            skLineSegment(sketch, "E387", {"start": v(19.35, 26.1) * mm, "end": v(18.86, 25.17) * mm});
            skLineSegment(sketch, "E388", {"start": v(18.86, 25.17) * mm, "end": v(18.44, 24.2) * mm});
            skLineSegment(sketch, "E389", {"start": v(18.44, 24.2) * mm, "end": v(18.1, 23.2) * mm});
            skLineSegment(sketch, "E390", {"start": v(18.1, 23.2) * mm, "end": v(17.82, 22.18) * mm});
            skLineSegment(sketch, "E391", {"start": v(17.82, 22.18) * mm, "end": v(17.63, 21.15) * mm});
            skLineSegment(sketch, "E392", {"start": v(17.63, 21.15) * mm, "end": v(17.5, 20.1) * mm});
            skLineSegment(sketch, "E393", {"start": v(17.5, 20.1) * mm, "end": v(17.46, 19.05) * mm});
            skLineSegment(sketch, "E394", {"start": v(17.46, 19.05) * mm, "end": v(17.5, 18.01) * mm});
            skLineSegment(sketch, "E395", {"start": v(17.5, 18.01) * mm, "end": v(17.63, 16.95) * mm});
            skLineSegment(sketch, "E396", {"start": v(17.63, 16.95) * mm, "end": v(17.82, 15.92) * mm});
            skLineSegment(sketch, "E397", {"start": v(17.82, 15.92) * mm, "end": v(18.1, 14.9) * mm});
            skLineSegment(sketch, "E398", {"start": v(18.1, 14.9) * mm, "end": v(18.44, 13.9) * mm});
            skLineSegment(sketch, "E399", {"start": v(18.44, 13.9) * mm, "end": v(18.86, 12.95) * mm});
            skLineSegment(sketch, "E400", {"start": v(18.86, 12.95) * mm, "end": v(19.35, 12.02) * mm});
            skLineSegment(sketch, "E401", {"start": v(19.35, 12.02) * mm, "end": v(19.9, 11.13) * mm});
            skLineSegment(sketch, "E402", {"start": v(19.9, 11.13) * mm, "end": v(20.53, 10.29) * mm});
            skLineSegment(sketch, "E403", {"start": v(20.53, 10.29) * mm, "end": v(21.2, 9.48) * mm});
            skLineSegment(sketch, "E404", {"start": v(21.2, 9.48) * mm, "end": v(21.95, 8.74) * mm});
            skLineSegment(sketch, "E405", {"start": v(21.95, 8.74) * mm, "end": v(22.75, 8.04) * mm});
            skLineSegment(sketch, "E406", {"start": v(22.75, 8.04) * mm, "end": v(23.58, 7.4) * mm});
            skLineSegment(sketch, "E407", {"start": v(23.58, 7.4) * mm, "end": v(24.47, 6.86) * mm});
            skLineSegment(sketch, "E408", {"start": v(24.47, 6.86) * mm, "end": v(25.4, 6.35) * mm});
            skSolve(sketch);
        }
        {
            var Q0;
            Q0=qCreatedBy(makeId("Top.planeOp"),FACE);
            var sketch = newSketch(context, id + "F1", { "sketchPlane" : qUnion([Q0])});
            skLineSegment(sketch, "E409.0", {"start": v(-25.4, 180.98) * mm, "end": v(-25.4, -180.98) * mm});
            skLineSegment(sketch, "E410.0", {"start": v(25.4, 180.98) * mm, "end": v(25.4, 31.75) * mm});
            skLineSegment(sketch, "E411.0", {"start": v(25.4, 6.35) * mm, "end": v(25.4, -180.98) * mm});
            skPoint(sketch, "E412.0", {"position": v(0, -173.04) * mm});
            skPoint(sketch, "E413.0", {"position": v(0, -188.91) * mm});
            skPoint(sketch, "E414.0", {"position": v(0, -96.84) * mm});
            skPoint(sketch, "E415.0", {"position": v(0, -112.71) * mm});
            skPoint(sketch, "E416.0", {"position": v(0, 115.89) * mm});
            skPoint(sketch, "E417.0", {"position": v(0, 93.66) * mm});
            skPoint(sketch, "E418.0", {"position": v(0, 193.68) * mm});
            skPoint(sketch, "E419.0", {"position": v(0, 168.28) * mm});
            skLineSegment(sketch, "E420", {"start": v(0, 193.68) * mm, "end": v(0, 168.28) * mm, "construction": true});
            skLineSegment(sketch, "E421", {"start": v(0, 115.89) * mm, "end": v(0, 93.66) * mm, "construction": true});
            skLineSegment(sketch, "E422", {"start": v(0, -96.84) * mm, "end": v(0, -112.71) * mm, "construction": true});
            skLineSegment(sketch, "E423", {"start": v(0, -173.04) * mm, "end": v(0, -188.91) * mm, "construction": true});
            skCircle(sketch, "E424", {"center": v(0, -104.78) * mm, "radius": 7.94 * mm});
            skCircle(sketch, "E425", {"center": v(0, -180.97) * mm, "radius": 7.94 * mm});
            skCircle(sketch, "E426", {"center": v(0, 104.78) * mm, "radius": 11.11 * mm});
            skCircle(sketch, "E427", {"center": v(0, 180.97) * mm, "radius": 12.7 * mm});
            skArc(sketch, "E428", {"start": v(-25.4, -180.98) * mm, "mid": v(0, -206.37) * mm, "end": v(25.4, -180.98) * mm});
            skArc(sketch, "E429", {"start": v(25.4, 180.98) * mm, "mid": v(0, 206.37) * mm, "end": v(-25.4, 180.98) * mm});
            skArc(sketch, "E430", {"start": v(25.4, 31.75) * mm, "mid": v(17.47, 19.05) * mm, "end": v(25.4, 6.35) * mm});
            skSolve(sketch);
        }
        {
            var Q0;
            Q0 = qSketchRegion(id + "F1", true);
            extrude(context, id + "F2", {"entities" : qUnion([Q0]), "depth" : 9.52 * mm, "offsetDistance" : 25.4 * mm});
        }
    });
